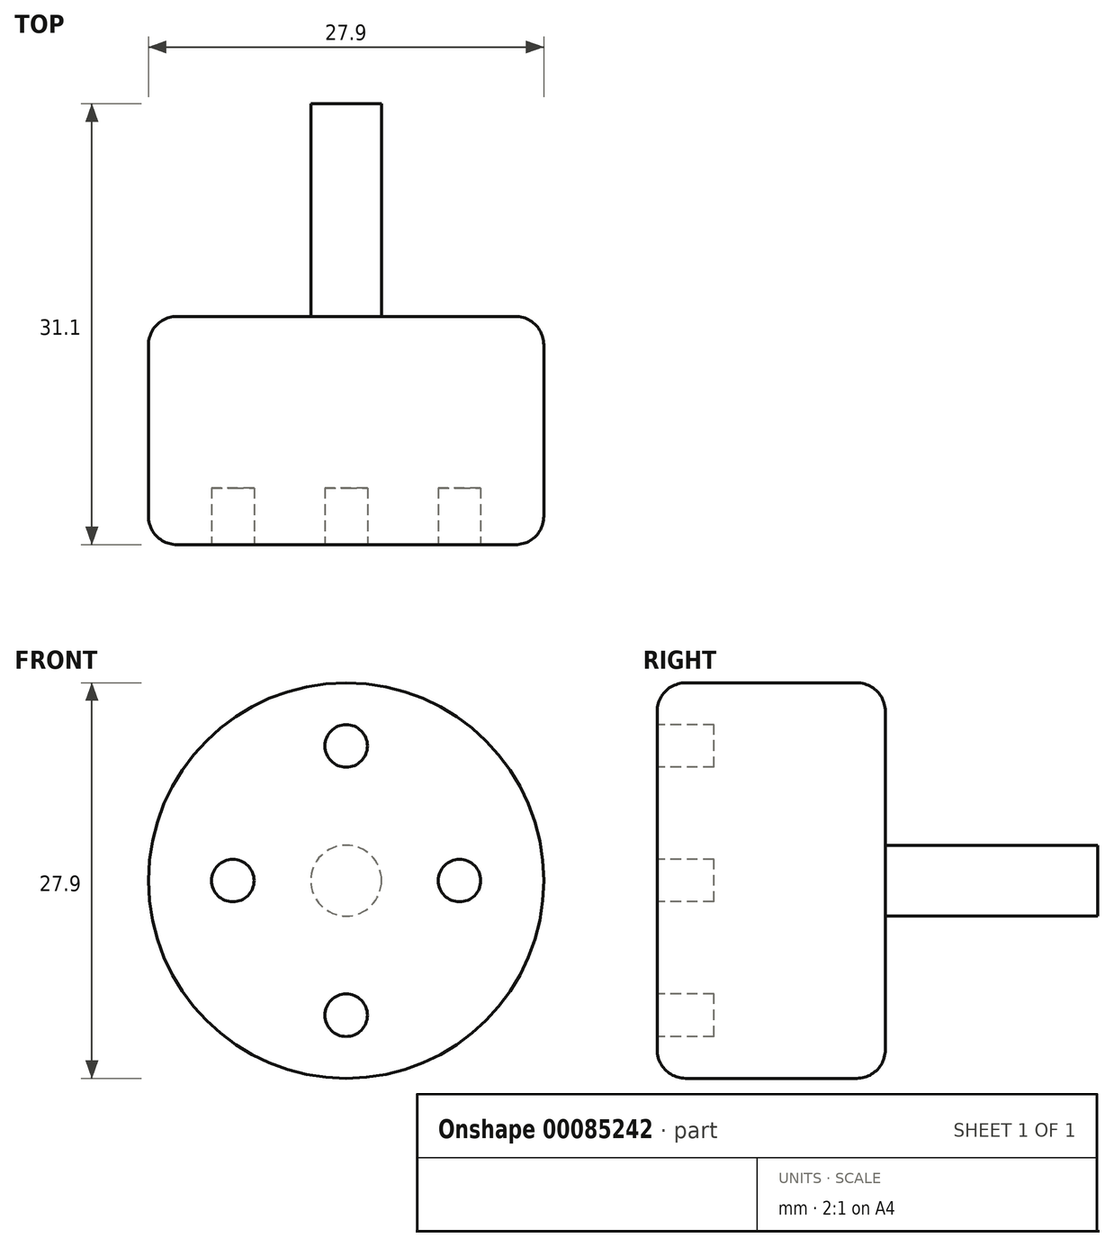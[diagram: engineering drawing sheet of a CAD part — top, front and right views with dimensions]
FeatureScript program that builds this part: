
annotation { "Feature Type Name" : "Feature", "Feature Type Description" : "" }
export const myFeature = defineFeature(function(context is Context, id is Id, definition is map)
    precondition{}
    {
        {
            var Q0;
            Q0=qCreatedBy(makeId("Front.planeOp"),FACE);
            var sketch = newSketch(context, id + "F0", { "sketchPlane" : qUnion([Q0])});
            skCircle(sketch, "E0", {"center": v(0, 0) * mm, "radius": 13.95 * mm});
            skSolve(sketch);
        }
        {
            var Q0;
            Q0 = qSketchRegion(id + "F0", true);
            extrude(context, id + "F1", {"entities" : qUnion([Q0]), "oppositeDirection" : true, "depth" : 16.1 * mm});
        }
        {
            var Q0;
            Q0=makeQuery(id+"F1.opExtrude","CAP_FACE",FACE,{"disambiguationData":[OSD([sQuery(id+"F0.wireOp",EDGE,"E0")])],"isStart":false});
            var sketch = newSketch(context, id + "F2", { "sketchPlane" : qUnion([Q0])});
            skCircle(sketch, "E1", {"center": v(0, 0) * mm, "radius": 2.5 * mm});
            skSolve(sketch);
        }
        {
            var Q0;
            Q0 = qSketchRegion(id + "F2", true);
            extrude(context, id + "F3", {"entities" : qUnion([Q0]), "operationType" : NewBodyOperationType.ADD, "depth" : 15 * mm});
        }
        {
            var Q0;
            Q0=makeQuery(id+"F1.opExtrude","CAP_FACE",FACE,{"disambiguationData":[OSD([sQuery(id+"F0.wireOp",EDGE,"E0")])],"isStart":true});
            var sketch = newSketch(context, id + "F4", { "sketchPlane" : qUnion([Q0])});
            skCircle(sketch, "E2", {"center": v(0, 0) * mm, "radius": 9.5 * mm, "construction": true});
            skCircle(sketch, "E3", {"center": v(0, 0) * mm, "radius": 8 * mm, "construction": true});
            skCircle(sketch, "E4", {"center": v(0, 9.5) * mm, "radius": 1.5 * mm});
            skCircle(sketch, "E5", {"center": v(0, -9.5) * mm, "radius": 1.5 * mm});
            skCircle(sketch, "E6", {"center": v(-8, 0) * mm, "radius": 1.5 * mm});
            skCircle(sketch, "E7", {"center": v(8, 0) * mm, "radius": 1.5 * mm});
            skSolve(sketch);
        }
        {
            var Q0;
            Q0 = qSketchRegion(id + "F4", true);
            extrude(context, id + "F5", {"entities" : qUnion([Q0]), "operationType" : NewBodyOperationType.REMOVE, "oppositeDirection" : true, "depth" : 4 * mm});
        }
        {
            var Q0;
            Q0=makeQuery(id+"F1.opExtrude","SWEPT_FACE",FACE,{"disambiguationData":[OSD([sQuery(id+"F0.wireOp",EDGE,"E0")])]});
            fillet(context, id + "F6", {"entities" : qUnion([Q0]), "radius" : 2 * mm, "tangentPropagation" : true, "allowEdgeOverflow" : false});
        }
    });
